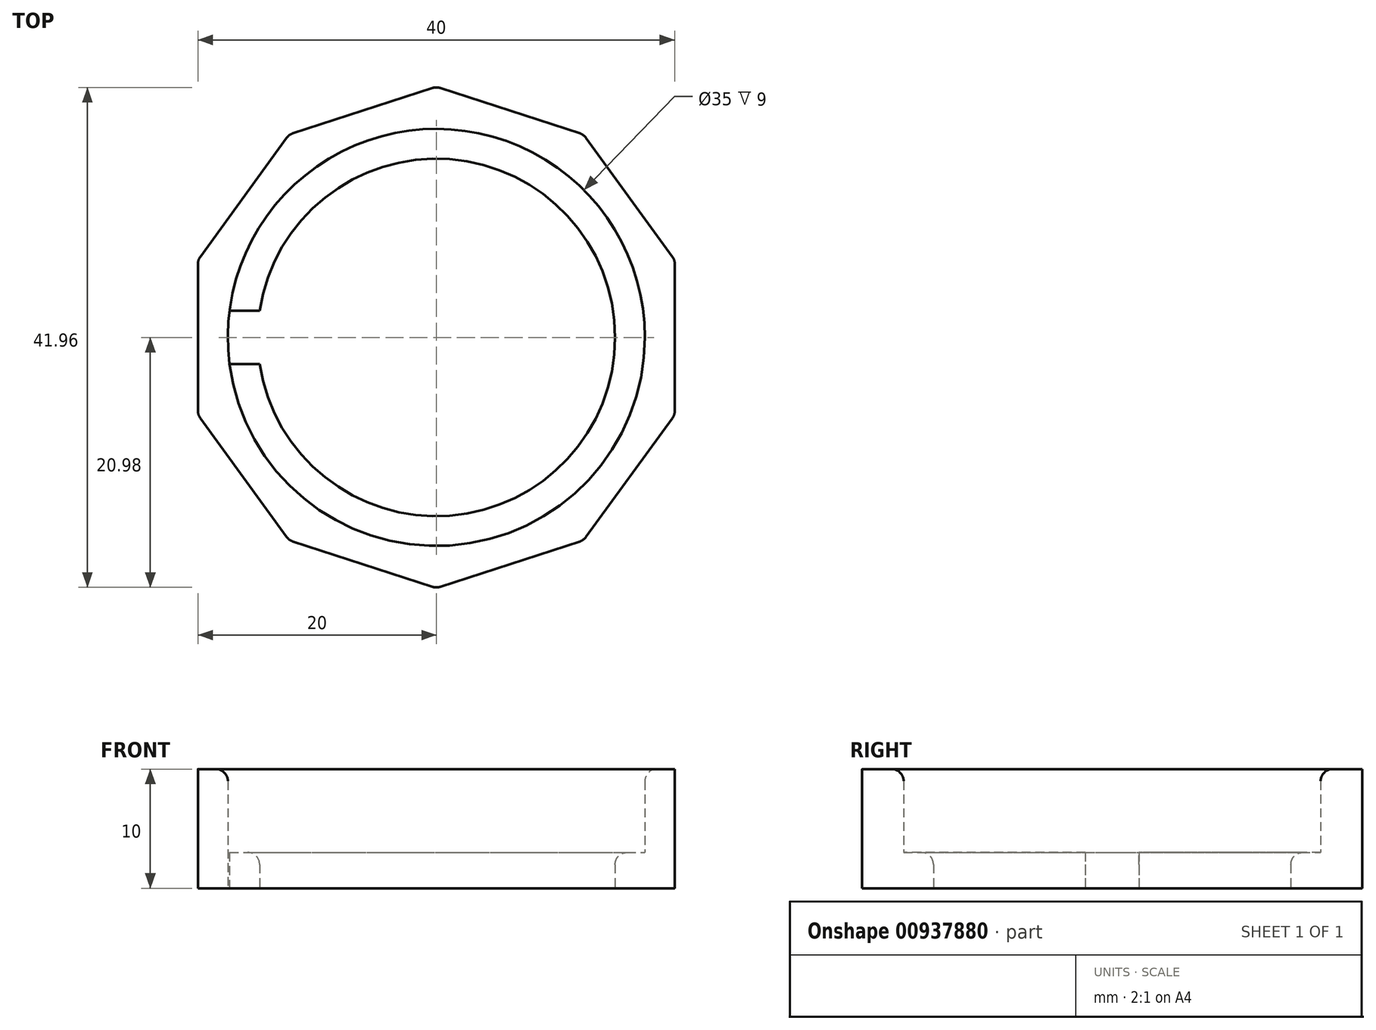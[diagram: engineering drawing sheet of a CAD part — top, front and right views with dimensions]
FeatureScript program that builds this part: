
annotation { "Feature Type Name" : "Feature", "Feature Type Description" : "" }
export const myFeature = defineFeature(function(context is Context, id is Id, definition is map)
    precondition{}
    {
        {
            var Q0;
            Q0=qCreatedBy(makeId("Top.planeOp"),FACE);
            var sketch = newSketch(context, id + "F0", { "sketchPlane" : qUnion([Q0])});
            skCircle(sketch, "E0", {"center": v(0, 0) * mm, "radius": 17.5 * mm});
            skCircle(sketch, "E1.cCircle", {"center": v(0, 0) * mm, "radius": 20 * mm, "construction": true});
            skLineSegment(sketch, "E1.0", {"start": v(20, -6.5) * mm, "end": v(12.36, -17.02) * mm});
            skLineSegment(sketch, "E1.1", {"start": v(12.36, -17.02) * mm, "end": v(0, -21.03) * mm});
            skLineSegment(sketch, "E1.2", {"start": v(0, -21.03) * mm, "end": v(-12.36, -17.02) * mm});
            skLineSegment(sketch, "E1.3", {"start": v(-12.36, -17.02) * mm, "end": v(-20, -6.5) * mm});
            skLineSegment(sketch, "E1.4", {"start": v(-20, -6.5) * mm, "end": v(-20, 6.5) * mm});
            skLineSegment(sketch, "E1.5", {"start": v(-20, 6.5) * mm, "end": v(-12.36, 17.02) * mm});
            skLineSegment(sketch, "E1.6", {"start": v(-12.36, 17.02) * mm, "end": v(0, 21.03) * mm});
            skLineSegment(sketch, "E1.7", {"start": v(0, 21.03) * mm, "end": v(12.36, 17.02) * mm});
            skLineSegment(sketch, "E1.8", {"start": v(12.36, 17.02) * mm, "end": v(20, 6.5) * mm});
            skLineSegment(sketch, "E1.9", {"start": v(20, 6.5) * mm, "end": v(20, -6.5) * mm});
            skPoint(sketch, "E1.0.midPoint", {"position": v(16.18, -11.76) * mm});
            skCircle(sketch, "E2", {"center": v(0, 0) * mm, "radius": 15 * mm});
            skLineSegment(sketch, "E3.bottom", {"start": v(-20, 2.25) * mm, "end": v(20, 2.25) * mm});
            skLineSegment(sketch, "E3.top", {"start": v(-20, -2.25) * mm, "end": v(20, -2.25) * mm});
            skLineSegment(sketch, "E3.left", {"start": v(-20, 2.25) * mm, "end": v(-20, -2.25) * mm});
            skLineSegment(sketch, "E3.right", {"start": v(20, 2.25) * mm, "end": v(20, -2.25) * mm});
            skSolve(sketch);
        }
        {
            var Q0;
            Q0 = qSketchRegion(id + "F0", true);
            extrude(context, id + "F1", {"entities" : qUnion([Q0]), "depth" : 10 * mm, "offsetDistance" : 25.4 * mm});
        }
        {
            var Q0;
            {var subQ0=sQuery(id+"F0.wireOp",EDGE,"E3.bottom");var subQ1=sQuery(id+"F0.wireOp",EDGE,"E0");var subQ2=makeQuery(id+"F0.imprint","INTERSECT",VERTEX,{"disambiguationData":[OD(0.0)],"derivedFrom":[subQ1,subQ0]});Q0=makeQuery(id+"F0.imprint","IMPRINT",FACE,{"disambiguationData":[TD([[makeQuery(id+"F0.imprint","IMPRINT",EDGE,{"disambiguationData":[TD([[subQ2,1.0]])],"derivedFrom":subQ1}),1.0]])]});}
            var Q1;
            {var subQ0=sQuery(id+"F0.wireOp",EDGE,"E3.top");var subQ1=sQuery(id+"F0.wireOp",EDGE,"E0");var subQ2=makeQuery(id+"F0.imprint","INTERSECT",VERTEX,{"disambiguationData":[OD(0.0)],"derivedFrom":[subQ1,subQ0]});Q1=makeQuery(id+"F0.imprint","IMPRINT",FACE,{"disambiguationData":[TD([[makeQuery(id+"F0.imprint","IMPRINT",EDGE,{"disambiguationData":[TD([[subQ2,-1.0]])],"derivedFrom":subQ1}),1.0]])]});}
            var Q2;
            {var subQ0=sQuery(id+"F0.wireOp",EDGE,"E3.bottom");var subQ1=sQuery(id+"F0.wireOp",EDGE,"E0");var subQ2=makeQuery(id+"F0.imprint","INTERSECT",VERTEX,{"disambiguationData":[OD(1.0)],"derivedFrom":[subQ1,subQ0]});Q2=makeQuery(id+"F0.imprint","IMPRINT",FACE,{"disambiguationData":[TD([[makeQuery(id+"F0.imprint","IMPRINT",EDGE,{"disambiguationData":[TD([[subQ2,1.0]])],"derivedFrom":subQ1}),1.0]])]});}
            extrude(context, id + "F2", {"entities" : qUnion([Q0, Q1, Q2]), "operationType" : NewBodyOperationType.ADD, "depth" : 3 * mm, "offsetDistance" : 25.4 * mm});
        }
        {
            var Q0;
            Q0=makeQuery(id+"F2.opExtrude","CAP_EDGE",EDGE,{"disambiguationData":[OSD([sQuery(id+"F0.wireOp",EDGE,"E2")])],"isStart":false});
            fillet(context, id + "F3", {"entities" : qUnion([Q0]), "radius" : 1 * mm, "tangentPropagation" : true, "allowEdgeOverflow" : false});
        }
        {
            var Q0;
            Q0=makeQuery(id+"F1.opExtrude","SWEPT_EDGE",EDGE,{"disambiguationData":[OSD([sQuery(id+"F0.wireOp",EDGE,"E1.0"),sQuery(id+"F0.wireOp",EDGE,"E1.9")])]});
            var Q1;
            Q1=makeQuery(id+"F1.opExtrude","SWEPT_EDGE",EDGE,{"disambiguationData":[OSD([sQuery(id+"F0.wireOp",EDGE,"E1.0"),sQuery(id+"F0.wireOp",EDGE,"E1.1")])]});
            var Q2;
            Q2=makeQuery(id+"F1.opExtrude","SWEPT_EDGE",EDGE,{"disambiguationData":[OSD([sQuery(id+"F0.wireOp",EDGE,"E1.1"),sQuery(id+"F0.wireOp",EDGE,"E1.2")])]});
            var Q3;
            Q3=makeQuery(id+"F1.opExtrude","SWEPT_EDGE",EDGE,{"disambiguationData":[OSD([sQuery(id+"F0.wireOp",EDGE,"E1.2"),sQuery(id+"F0.wireOp",EDGE,"E1.3")])]});
            var Q4;
            Q4=makeQuery(id+"F1.opExtrude","SWEPT_EDGE",EDGE,{"disambiguationData":[OSD([sQuery(id+"F0.wireOp",EDGE,"E1.3"),sQuery(id+"F0.wireOp",EDGE,"E1.4")])]});
            var Q5;
            Q5=makeQuery(id+"F1.opExtrude","SWEPT_EDGE",EDGE,{"disambiguationData":[OSD([sQuery(id+"F0.wireOp",EDGE,"E1.4"),sQuery(id+"F0.wireOp",EDGE,"E1.5")])]});
            var Q6;
            Q6=makeQuery(id+"F1.opExtrude","SWEPT_EDGE",EDGE,{"disambiguationData":[OSD([sQuery(id+"F0.wireOp",EDGE,"E1.6"),sQuery(id+"F0.wireOp",EDGE,"E1.7")])]});
            var Q7;
            Q7=makeQuery(id+"F1.opExtrude","SWEPT_EDGE",EDGE,{"disambiguationData":[OSD([sQuery(id+"F0.wireOp",EDGE,"E1.5"),sQuery(id+"F0.wireOp",EDGE,"E1.6")])]});
            var Q8;
            Q8=makeQuery(id+"F1.opExtrude","SWEPT_EDGE",EDGE,{"disambiguationData":[OSD([sQuery(id+"F0.wireOp",EDGE,"E1.7"),sQuery(id+"F0.wireOp",EDGE,"E1.8")])]});
            var Q9;
            Q9=makeQuery(id+"F1.opExtrude","SWEPT_EDGE",EDGE,{"disambiguationData":[OSD([sQuery(id+"F0.wireOp",EDGE,"E1.8"),sQuery(id+"F0.wireOp",EDGE,"E1.9")])]});
            fillet(context, id + "F4", {"entities" : qUnion([Q0, Q1, Q2, Q3, Q4, Q5, Q6, Q7, Q8, Q9]), "radius" : 1 * mm, "tangentPropagation" : true, "allowEdgeOverflow" : false});
        }
        {
            var Q0;
            Q0=makeQuery(id+"F1.opExtrude","CAP_EDGE",EDGE,{"disambiguationData":[OSD([sQuery(id+"F0.wireOp",EDGE,"E0")])],"isStart":false});
            fillet(context, id + "F5", {"entities" : qUnion([Q0]), "radius" : 1 * mm, "tangentPropagation" : true, "allowEdgeOverflow" : false});
        }
    });
